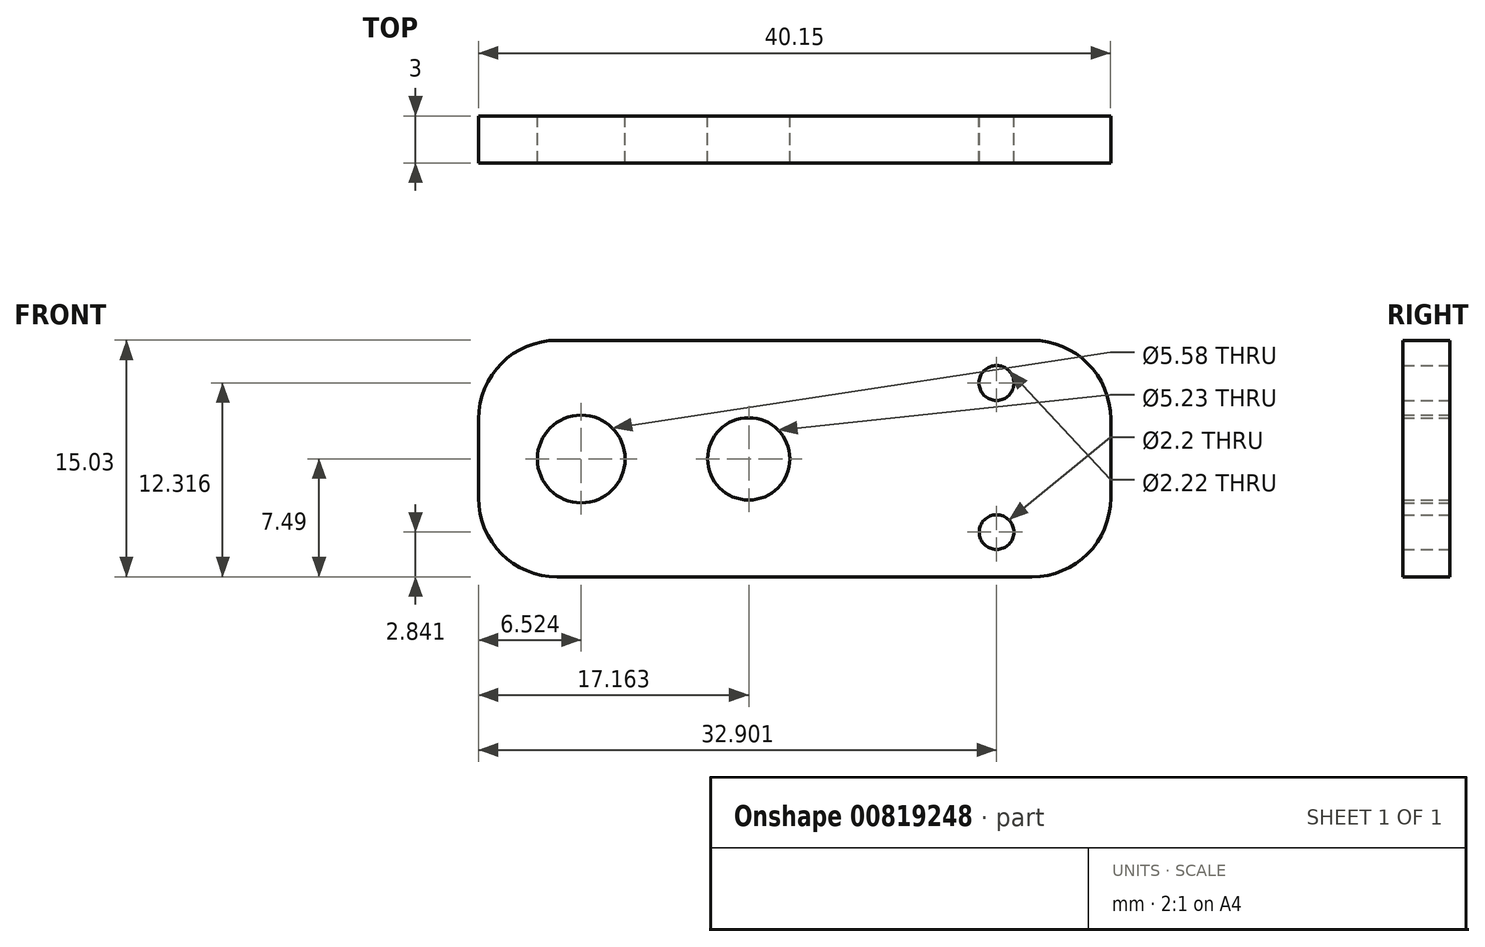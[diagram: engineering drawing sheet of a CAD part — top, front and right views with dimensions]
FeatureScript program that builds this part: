
annotation { "Feature Type Name" : "Feature", "Feature Type Description" : "" }
export const myFeature = defineFeature(function(context is Context, id is Id, definition is map)
    precondition{}
    {
        {
            var Q0;
            Q0=qCreatedBy(makeId("Front.planeOp"),FACE);
            var sketch = newSketch(context, id + "F0", { "sketchPlane" : qUnion([Q0])});
            skLineSegment(sketch, "E0.bottom", {"start": v(-15.12, 7.54) * mm, "end": v(15.03, 7.54) * mm});
            skLineSegment(sketch, "E0.top", {"start": v(-15.12, -7.5) * mm, "end": v(15.03, -7.5) * mm});
            skLineSegment(sketch, "E0.left", {"start": v(-20.12, 2.54) * mm, "end": v(-20.12, -2.5) * mm});
            skLineSegment(sketch, "E0.right", {"start": v(20.03, 2.54) * mm, "end": v(20.03, -2.5) * mm});
            skPoint(sketch, "E1.visualSharp", {"position": v(-20.12, 7.54) * mm});
            skArc(sketch, "E1.filletArc", {"start": v(-15.12, 7.54) * mm, "mid": v(-18.66, 6.07) * mm, "end": v(-20.12, 2.54) * mm});
            skPoint(sketch, "E2.visualSharp", {"position": v(-20.12, -7.5) * mm});
            skArc(sketch, "E2.filletArc", {"start": v(-20.12, -2.5) * mm, "mid": v(-18.66, -6.03) * mm, "end": v(-15.12, -7.5) * mm});
            skPoint(sketch, "E3.visualSharp", {"position": v(20.03, -7.5) * mm});
            skArc(sketch, "E3.filletArc", {"start": v(15.03, -7.5) * mm, "mid": v(18.57, -6.03) * mm, "end": v(20.03, -2.5) * mm});
            skPoint(sketch, "E4.visualSharp", {"position": v(20.03, 7.54) * mm});
            skArc(sketch, "E4.filletArc", {"start": v(20.03, 2.54) * mm, "mid": v(18.57, 6.07) * mm, "end": v(15.03, 7.54) * mm});
            skCircle(sketch, "E5", {"center": v(-13.6, 0) * mm, "radius": 2.79 * mm});
            skCircle(sketch, "E6", {"center": v(-2.96, 0) * mm, "radius": 2.61 * mm});
            skSolve(sketch);
        }
        {
            var Q0;
            Q0 = qSketchRegion(id + "F0", true);
            extrude(context, id + "F1", {"entities" : qUnion([Q0]), "depth" : 3 * mm, "offsetDistance" : 25 * mm});
        }
        {
            var Q0;
            Q0=makeQuery(id+"F1.opExtrude","CAP_FACE",FACE,{"disambiguationData":[OSD([sQuery(id+"F0.wireOp",EDGE,"E0.bottom"),sQuery(id+"F0.wireOp",EDGE,"E0.top"),sQuery(id+"F0.wireOp",EDGE,"E0.left"),sQuery(id+"F0.wireOp",EDGE,"E0.right"),sQuery(id+"F0.wireOp",EDGE,"E1.filletArc"),sQuery(id+"F0.wireOp",EDGE,"E2.filletArc"),sQuery(id+"F0.wireOp",EDGE,"E3.filletArc"),sQuery(id+"F0.wireOp",EDGE,"E4.filletArc"),sQuery(id+"F0.wireOp",EDGE,"E5"),sQuery(id+"F0.wireOp",EDGE,"E6")])],"isStart":true});
            var sketch = newSketch(context, id + "F2", { "sketchPlane" : qUnion([Q0])});
            skCircle(sketch, "E7", {"center": v(-12.78, 4.83) * mm, "radius": 1.11 * mm});
            skCircle(sketch, "E8", {"center": v(-12.78, -4.65) * mm, "radius": 1.1 * mm});
            skSolve(sketch);
        }
        {
            var Q0;
            Q0 = qSketchRegion(id + "F2", true);
            extrude(context, id + "F3", {"entities" : qUnion([Q0]), "operationType" : NewBodyOperationType.REMOVE, "oppositeDirection" : true, "depth" : 25 * mm, "offsetDistance" : 25 * mm});
        }
    });
